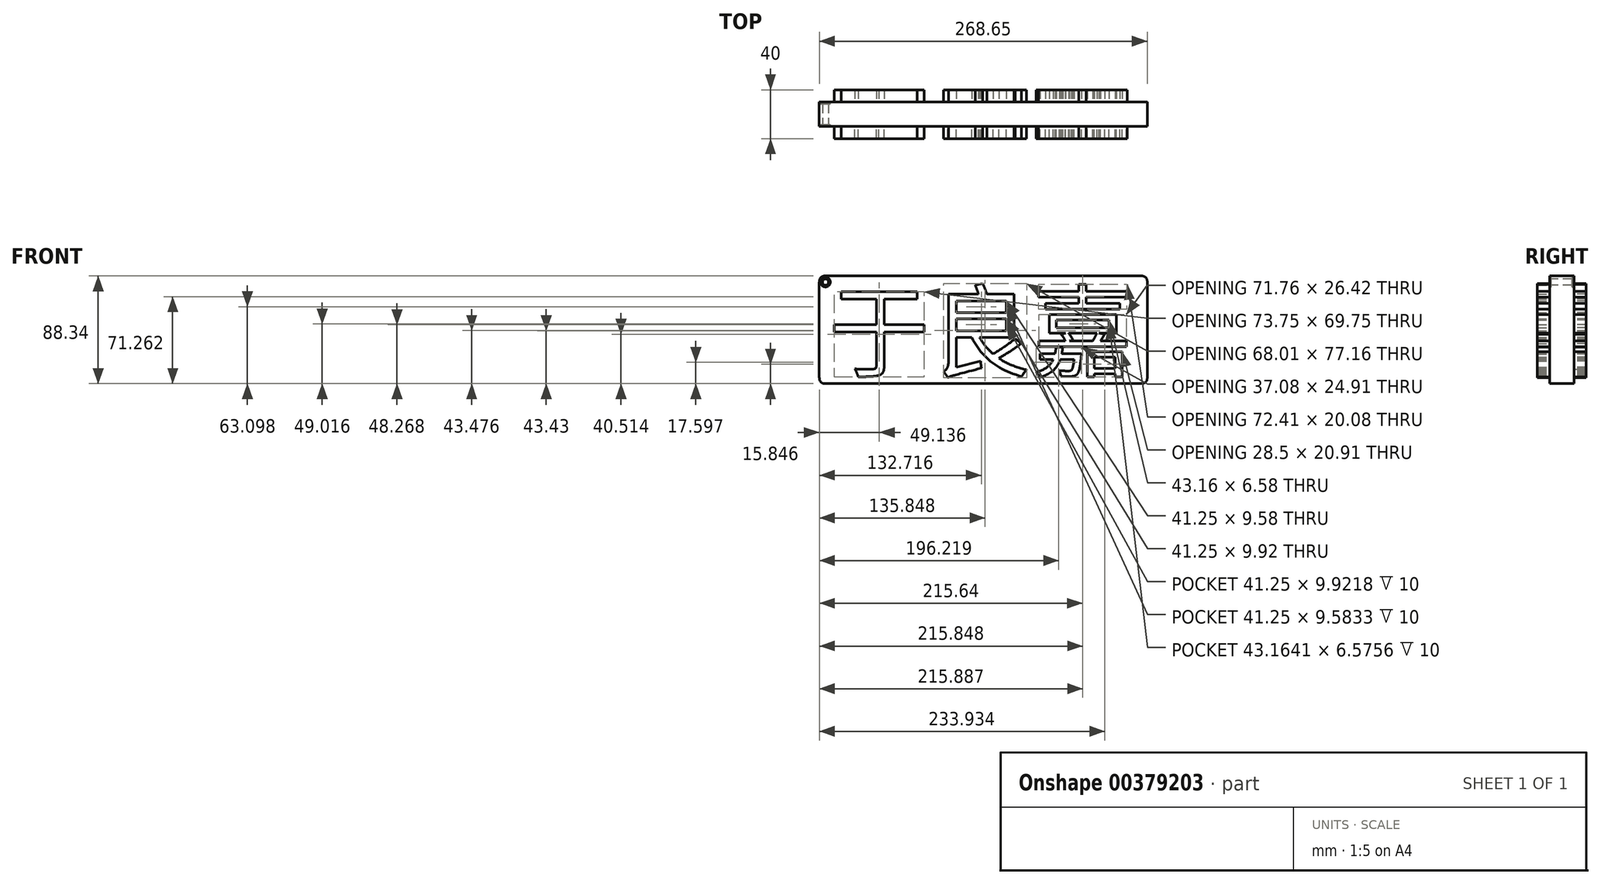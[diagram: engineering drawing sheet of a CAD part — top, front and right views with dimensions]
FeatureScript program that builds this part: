
annotation { "Feature Type Name" : "Feature", "Feature Type Description" : "" }
export const myFeature = defineFeature(function(context is Context, id is Id, definition is map)
    precondition{}
    {
        {
            var Q0;
            Q0=qCreatedBy(makeId("Front.planeOp"),FACE);
            var sketch = newSketch(context, id + "F0", { "sketchPlane" : qUnion([Q0])});
            skText(sketch, "E0", { "text": "于良嘉", "fontName": "NotoSansCJKtc-Regular.otf"});
            const initialGuessF0  = {"E0": [-0.12466, -0.0336, 1, 0, 0.06]};
            skSetInitialGuess(sketch, initialGuessF0);
            skSolve(sketch);
        }
        {
            var Q0;
            Q0 = qSketchRegion(id + "F0", true);
            extrude(context, id + "F1", {"entities" : qUnion([Q0]), "depth" : 20 * mm});
        }
        {
            var Q0;
            Q0=qCreatedBy(makeId("Front.planeOp"),FACE);
            var sketch = newSketch(context, id + "F2", { "sketchPlane" : qUnion([Q0])});
            skLineSegment(sketch, "E1.bottom", {"start": v(-132.1, 43.1) * mm, "end": v(136.56, 43.1) * mm});
            skLineSegment(sketch, "E1.top", {"start": v(-132.1, -45.24) * mm, "end": v(136.56, -45.24) * mm});
            skLineSegment(sketch, "E1.left", {"start": v(-132.1, 43.1) * mm, "end": v(-132.1, -45.24) * mm});
            skLineSegment(sketch, "E1.right", {"start": v(136.56, 43.1) * mm, "end": v(136.56, -45.24) * mm});
            skSolve(sketch);
        }
        {
            var Q0;
            Q0=makeQuery(id+"F2.imprint","IMPRINT",FACE,{"disambiguationData":[TD([[makeQuery(id+"F2.imprint","IMPRINT",EDGE,{"derivedFrom":sQuery(id+"F2.wireOp",EDGE,"E1.bottom")}),-1.0]])]});
            extrude(context, id + "F3", {"entities" : qUnion([Q0]), "depth" : 10 * mm});
        }
        {
            var Q0;
            Q0=makeQuery(id+"F3.opExtrude","SWEPT_EDGE",EDGE,{"disambiguationData":[OSD([sQuery(id+"F2.wireOp",EDGE,"E1.top"),sQuery(id+"F2.wireOp",EDGE,"E1.left")])]});
            fillet(context, id + "F4", {"entities" : qUnion([Q0]), "radius" : 5.08 * mm, "tangentPropagation" : true, "rho" : 0.5, "crossSection" : FilletCrossSection.CONIC, "allowEdgeOverflow" : false});
        }
        {
            var Q0;
            Q0=makeQuery(id+"F3.opExtrude","SWEPT_EDGE",EDGE,{"disambiguationData":[OSD([sQuery(id+"F2.wireOp",EDGE,"E1.bottom"),sQuery(id+"F2.wireOp",EDGE,"E1.left")])]});
            fillet(context, id + "F5", {"entities" : qUnion([Q0]), "radius" : 5.08 * mm, "tangentPropagation" : true, "rho" : 0.5, "crossSection" : FilletCrossSection.CONIC, "allowEdgeOverflow" : false});
        }
        {
            var Q0;
            Q0=makeQuery(id+"F3.opExtrude","SWEPT_EDGE",EDGE,{"disambiguationData":[OSD([sQuery(id+"F2.wireOp",EDGE,"E1.top"),sQuery(id+"F2.wireOp",EDGE,"E1.right")])]});
            fillet(context, id + "F6", {"entities" : qUnion([Q0]), "radius" : 5.08 * mm, "tangentPropagation" : true, "rho" : 0.5, "crossSection" : FilletCrossSection.CONIC, "allowEdgeOverflow" : false});
        }
        {
            var Q0;
            Q0=makeQuery(id+"F3.opExtrude","SWEPT_EDGE",EDGE,{"disambiguationData":[OSD([sQuery(id+"F2.wireOp",EDGE,"E1.bottom"),sQuery(id+"F2.wireOp",EDGE,"E1.right")])]});
            fillet(context, id + "F7", {"entities" : qUnion([Q0]), "radius" : 5.08 * mm, "tangentPropagation" : true, "rho" : 0.5, "crossSection" : FilletCrossSection.CONIC, "allowEdgeOverflow" : false});
        }
        {
            var Q0;
            Q0=makeQuery(id+"F1.opExtrude","SWEPT_BODY",BODY,{"disambiguationData":[OSD([sQuery(id+"F0.wireOp",EDGE,"E0.sketch_text.stroke-69"),sQuery(id+"F0.wireOp",EDGE,"E0.sketch_text.stroke-70"),sQuery(id+"F0.wireOp",EDGE,"E0.sketch_text.stroke-71"),sQuery(id+"F0.wireOp",EDGE,"E0.sketch_text.stroke-72"),sQuery(id+"F0.wireOp",EDGE,"E0.sketch_text.stroke-73"),sQuery(id+"F0.wireOp",EDGE,"E0.sketch_text.stroke-74"),sQuery(id+"F0.wireOp",EDGE,"E0.sketch_text.stroke-75"),sQuery(id+"F0.wireOp",EDGE,"E0.sketch_text.stroke-76"),sQuery(id+"F0.wireOp",EDGE,"E0.sketch_text.stroke-77"),sQuery(id+"F0.wireOp",EDGE,"E0.sketch_text.stroke-78"),sQuery(id+"F0.wireOp",EDGE,"E0.sketch_text.stroke-79"),sQuery(id+"F0.wireOp",EDGE,"E0.sketch_text.stroke-80")])]});
            var Q1;
            Q1=makeQuery(id+"F1.opExtrude","SWEPT_BODY",BODY,{"disambiguationData":[OSD([sQuery(id+"F0.wireOp",EDGE,"E0.sketch_text.stroke-81"),sQuery(id+"F0.wireOp",EDGE,"E0.sketch_text.stroke-82"),sQuery(id+"F0.wireOp",EDGE,"E0.sketch_text.stroke-83"),sQuery(id+"F0.wireOp",EDGE,"E0.sketch_text.stroke-84"),sQuery(id+"F0.wireOp",EDGE,"E0.sketch_text.stroke-85"),sQuery(id+"F0.wireOp",EDGE,"E0.sketch_text.stroke-86"),sQuery(id+"F0.wireOp",EDGE,"E0.sketch_text.stroke-87"),sQuery(id+"F0.wireOp",EDGE,"E0.sketch_text.stroke-88"),sQuery(id+"F0.wireOp",EDGE,"E0.sketch_text.stroke-89"),sQuery(id+"F0.wireOp",EDGE,"E0.sketch_text.stroke-90"),sQuery(id+"F0.wireOp",EDGE,"E0.sketch_text.stroke-91"),sQuery(id+"F0.wireOp",EDGE,"E0.sketch_text.stroke-92"),sQuery(id+"F0.wireOp",EDGE,"E0.sketch_text.stroke-93"),sQuery(id+"F0.wireOp",EDGE,"E0.sketch_text.stroke-94"),sQuery(id+"F0.wireOp",EDGE,"E0.sketch_text.stroke-95"),sQuery(id+"F0.wireOp",EDGE,"E0.sketch_text.stroke-96"),sQuery(id+"F0.wireOp",EDGE,"E0.sketch_text.stroke-97"),sQuery(id+"F0.wireOp",EDGE,"E0.sketch_text.stroke-98"),sQuery(id+"F0.wireOp",EDGE,"E0.sketch_text.stroke-99"),sQuery(id+"F0.wireOp",EDGE,"E0.sketch_text.stroke-100"),sQuery(id+"F0.wireOp",EDGE,"E0.sketch_text.stroke-101"),sQuery(id+"F0.wireOp",EDGE,"E0.sketch_text.stroke-102"),sQuery(id+"F0.wireOp",EDGE,"E0.sketch_text.stroke-103")])]});
            var Q2;
            Q2=makeQuery(id+"F1.opExtrude","SWEPT_BODY",BODY,{"disambiguationData":[OSD([sQuery(id+"F0.wireOp",EDGE,"E0.sketch_text.stroke-104"),sQuery(id+"F0.wireOp",EDGE,"E0.sketch_text.stroke-105"),sQuery(id+"F0.wireOp",EDGE,"E0.sketch_text.stroke-106"),sQuery(id+"F0.wireOp",EDGE,"E0.sketch_text.stroke-107"),sQuery(id+"F0.wireOp",EDGE,"E0.sketch_text.stroke-108"),sQuery(id+"F0.wireOp",EDGE,"E0.sketch_text.stroke-109"),sQuery(id+"F0.wireOp",EDGE,"E0.sketch_text.stroke-110"),sQuery(id+"F0.wireOp",EDGE,"E0.sketch_text.stroke-111"),sQuery(id+"F0.wireOp",EDGE,"E0.sketch_text.stroke-112"),sQuery(id+"F0.wireOp",EDGE,"E0.sketch_text.stroke-113"),sQuery(id+"F0.wireOp",EDGE,"E0.sketch_text.stroke-114"),sQuery(id+"F0.wireOp",EDGE,"E0.sketch_text.stroke-115"),sQuery(id+"F0.wireOp",EDGE,"E0.sketch_text.stroke-116"),sQuery(id+"F0.wireOp",EDGE,"E0.sketch_text.stroke-117"),sQuery(id+"F0.wireOp",EDGE,"E0.sketch_text.stroke-118"),sQuery(id+"F0.wireOp",EDGE,"E0.sketch_text.stroke-119")])]});
            var Q3;
            Q3=makeQuery(id+"F3.opExtrude","SWEPT_BODY",BODY,{"disambiguationData":[OSD([sQuery(id+"F2.wireOp",EDGE,"E1.bottom"),sQuery(id+"F2.wireOp",EDGE,"E1.top"),sQuery(id+"F2.wireOp",EDGE,"E1.left"),sQuery(id+"F2.wireOp",EDGE,"E1.right")])]});
            var Q4;
            Q4=makeQuery(id+"F1.opExtrude","SWEPT_BODY",BODY,{"disambiguationData":[OSD([sQuery(id+"F0.wireOp",EDGE,"E0.sketch_text.stroke-50"),sQuery(id+"F0.wireOp",EDGE,"E0.sketch_text.stroke-51"),sQuery(id+"F0.wireOp",EDGE,"E0.sketch_text.stroke-52"),sQuery(id+"F0.wireOp",EDGE,"E0.sketch_text.stroke-53"),sQuery(id+"F0.wireOp",EDGE,"E0.sketch_text.stroke-54"),sQuery(id+"F0.wireOp",EDGE,"E0.sketch_text.stroke-55"),sQuery(id+"F0.wireOp",EDGE,"E0.sketch_text.stroke-56"),sQuery(id+"F0.wireOp",EDGE,"E0.sketch_text.stroke-57"),sQuery(id+"F0.wireOp",EDGE,"E0.sketch_text.stroke-58"),sQuery(id+"F0.wireOp",EDGE,"E0.sketch_text.stroke-59"),sQuery(id+"F0.wireOp",EDGE,"E0.sketch_text.stroke-60"),sQuery(id+"F0.wireOp",EDGE,"E0.sketch_text.stroke-61"),sQuery(id+"F0.wireOp",EDGE,"E0.sketch_text.stroke-62"),sQuery(id+"F0.wireOp",EDGE,"E0.sketch_text.stroke-63"),sQuery(id+"F0.wireOp",EDGE,"E0.sketch_text.stroke-64"),sQuery(id+"F0.wireOp",EDGE,"E0.sketch_text.stroke-65"),sQuery(id+"F0.wireOp",EDGE,"E0.sketch_text.stroke-66"),sQuery(id+"F0.wireOp",EDGE,"E0.sketch_text.stroke-67"),sQuery(id+"F0.wireOp",EDGE,"E0.sketch_text.stroke-68")])]});
            var Q5;
            Q5=makeQuery(id+"F1.opExtrude","SWEPT_BODY",BODY,{"disambiguationData":[OSD([sQuery(id+"F0.wireOp",EDGE,"E0.sketch_text.stroke-20"),sQuery(id+"F0.wireOp",EDGE,"E0.sketch_text.stroke-21"),sQuery(id+"F0.wireOp",EDGE,"E0.sketch_text.stroke-22"),sQuery(id+"F0.wireOp",EDGE,"E0.sketch_text.stroke-23"),sQuery(id+"F0.wireOp",EDGE,"E0.sketch_text.stroke-24"),sQuery(id+"F0.wireOp",EDGE,"E0.sketch_text.stroke-25"),sQuery(id+"F0.wireOp",EDGE,"E0.sketch_text.stroke-26"),sQuery(id+"F0.wireOp",EDGE,"E0.sketch_text.stroke-27"),sQuery(id+"F0.wireOp",EDGE,"E0.sketch_text.stroke-28"),sQuery(id+"F0.wireOp",EDGE,"E0.sketch_text.stroke-29"),sQuery(id+"F0.wireOp",EDGE,"E0.sketch_text.stroke-30"),sQuery(id+"F0.wireOp",EDGE,"E0.sketch_text.stroke-31"),sQuery(id+"F0.wireOp",EDGE,"E0.sketch_text.stroke-32"),sQuery(id+"F0.wireOp",EDGE,"E0.sketch_text.stroke-33"),sQuery(id+"F0.wireOp",EDGE,"E0.sketch_text.stroke-34"),sQuery(id+"F0.wireOp",EDGE,"E0.sketch_text.stroke-35"),sQuery(id+"F0.wireOp",EDGE,"E0.sketch_text.stroke-36"),sQuery(id+"F0.wireOp",EDGE,"E0.sketch_text.stroke-37"),sQuery(id+"F0.wireOp",EDGE,"E0.sketch_text.stroke-38"),sQuery(id+"F0.wireOp",EDGE,"E0.sketch_text.stroke-39"),sQuery(id+"F0.wireOp",EDGE,"E0.sketch_text.stroke-40"),sQuery(id+"F0.wireOp",EDGE,"E0.sketch_text.stroke-41"),sQuery(id+"F0.wireOp",EDGE,"E0.sketch_text.stroke-42"),sQuery(id+"F0.wireOp",EDGE,"E0.sketch_text.stroke-43"),sQuery(id+"F0.wireOp",EDGE,"E0.sketch_text.stroke-44"),sQuery(id+"F0.wireOp",EDGE,"E0.sketch_text.stroke-45"),sQuery(id+"F0.wireOp",EDGE,"E0.sketch_text.stroke-46"),sQuery(id+"F0.wireOp",EDGE,"E0.sketch_text.stroke-47"),sQuery(id+"F0.wireOp",EDGE,"E0.sketch_text.stroke-48"),sQuery(id+"F0.wireOp",EDGE,"E0.sketch_text.stroke-49")])]});
            var Q6;
            Q6=makeQuery(id+"F1.opExtrude","SWEPT_BODY",BODY,{"disambiguationData":[OSD([sQuery(id+"F0.wireOp",EDGE,"E0.sketch_text.stroke-0"),sQuery(id+"F0.wireOp",EDGE,"E0.sketch_text.stroke-1"),sQuery(id+"F0.wireOp",EDGE,"E0.sketch_text.stroke-2"),sQuery(id+"F0.wireOp",EDGE,"E0.sketch_text.stroke-3"),sQuery(id+"F0.wireOp",EDGE,"E0.sketch_text.stroke-4"),sQuery(id+"F0.wireOp",EDGE,"E0.sketch_text.stroke-5"),sQuery(id+"F0.wireOp",EDGE,"E0.sketch_text.stroke-6"),sQuery(id+"F0.wireOp",EDGE,"E0.sketch_text.stroke-7"),sQuery(id+"F0.wireOp",EDGE,"E0.sketch_text.stroke-8"),sQuery(id+"F0.wireOp",EDGE,"E0.sketch_text.stroke-9"),sQuery(id+"F0.wireOp",EDGE,"E0.sketch_text.stroke-10"),sQuery(id+"F0.wireOp",EDGE,"E0.sketch_text.stroke-11"),sQuery(id+"F0.wireOp",EDGE,"E0.sketch_text.stroke-12"),sQuery(id+"F0.wireOp",EDGE,"E0.sketch_text.stroke-13"),sQuery(id+"F0.wireOp",EDGE,"E0.sketch_text.stroke-14"),sQuery(id+"F0.wireOp",EDGE,"E0.sketch_text.stroke-15"),sQuery(id+"F0.wireOp",EDGE,"E0.sketch_text.stroke-16"),sQuery(id+"F0.wireOp",EDGE,"E0.sketch_text.stroke-17"),sQuery(id+"F0.wireOp",EDGE,"E0.sketch_text.stroke-18"),sQuery(id+"F0.wireOp",EDGE,"E0.sketch_text.stroke-19")])]});
            booleanBodies(context, id + "F8", {"operationType" : BooleanOperationType.UNION, "tools" : qUnion([Q0, Q1, Q2, Q3, Q4, Q5, Q6])});
        }
        {
            var Q0;
            {var subQ0=sQuery(id+"F2.wireOp",EDGE,"E1.right");var subQ1=sQuery(id+"F2.wireOp",EDGE,"E1.bottom");var subQ2=sQuery(id+"F2.wireOp",EDGE,"E1.top");var subQ3=sQuery(id+"F2.wireOp",EDGE,"E1.left");Q0=makeQuery(id+"F8.opBoolean","SPLIT",FACE,{"disambiguationData":[TD([makeQuery(id+"F1.opExtrude","SWEPT_FACE",FACE,{"disambiguationData":[OSD([sQuery(id+"F0.wireOp",EDGE,"E0.sketch_text.stroke-0")])]})])],"derivedFrom":makeQuery(id+"F3.opExtrude","CAP_FACE",FACE,{"disambiguationData":[OSD([subQ1,subQ2,subQ3,subQ0])],"isStart":false})});}
            var sketch = newSketch(context, id + "F9", { "sketchPlane" : qUnion([Q0])});
            skCircle(sketch, "E2", {"center": v(-127.01, 38.04) * mm, "radius": 2.84 * mm});
            skSolve(sketch);
        }
        {
            var Q0;
            Q0=sQuery(id+"F9.wireOp",VERTEX,"E2.center");
            var Q1;
            Q1=makeQuery(id+"F1.opExtrude","SWEPT_BODY",BODY,{"disambiguationData":[OSD([sQuery(id+"F0.wireOp",EDGE,"E0.sketch_text.stroke-69"),sQuery(id+"F0.wireOp",EDGE,"E0.sketch_text.stroke-70"),sQuery(id+"F0.wireOp",EDGE,"E0.sketch_text.stroke-71"),sQuery(id+"F0.wireOp",EDGE,"E0.sketch_text.stroke-72"),sQuery(id+"F0.wireOp",EDGE,"E0.sketch_text.stroke-73"),sQuery(id+"F0.wireOp",EDGE,"E0.sketch_text.stroke-74"),sQuery(id+"F0.wireOp",EDGE,"E0.sketch_text.stroke-75"),sQuery(id+"F0.wireOp",EDGE,"E0.sketch_text.stroke-76"),sQuery(id+"F0.wireOp",EDGE,"E0.sketch_text.stroke-77"),sQuery(id+"F0.wireOp",EDGE,"E0.sketch_text.stroke-78"),sQuery(id+"F0.wireOp",EDGE,"E0.sketch_text.stroke-79"),sQuery(id+"F0.wireOp",EDGE,"E0.sketch_text.stroke-80")])]});
            hole(context, id + "F10", {"style" : HoleStyle.C_BORE, "endStyle" : HoleEndStyle.THROUGH, "holeDiameter" : 5 * mm, "cBoreDiameter" : 8 * mm, "cBoreDepth" : 1.5 * mm, "isTappedThrough" : true, "tappedDepth" : 12.7 * mm, "tapClearance" : 3, "startFromSketch" : true, "locations" : qUnion([Q0]), "scope" : qUnion([Q1])});
        }
        {
            var Q0;
            Q0=makeQuery(id+"F1.opExtrude","SWEPT_BODY",BODY,{"disambiguationData":[OSD([sQuery(id+"F0.wireOp",EDGE,"E0.sketch_text.stroke-69"),sQuery(id+"F0.wireOp",EDGE,"E0.sketch_text.stroke-70"),sQuery(id+"F0.wireOp",EDGE,"E0.sketch_text.stroke-71"),sQuery(id+"F0.wireOp",EDGE,"E0.sketch_text.stroke-72"),sQuery(id+"F0.wireOp",EDGE,"E0.sketch_text.stroke-73"),sQuery(id+"F0.wireOp",EDGE,"E0.sketch_text.stroke-74"),sQuery(id+"F0.wireOp",EDGE,"E0.sketch_text.stroke-75"),sQuery(id+"F0.wireOp",EDGE,"E0.sketch_text.stroke-76"),sQuery(id+"F0.wireOp",EDGE,"E0.sketch_text.stroke-77"),sQuery(id+"F0.wireOp",EDGE,"E0.sketch_text.stroke-78"),sQuery(id+"F0.wireOp",EDGE,"E0.sketch_text.stroke-79"),sQuery(id+"F0.wireOp",EDGE,"E0.sketch_text.stroke-80")])]});
            var Q1;
            Q1=makeQuery(id+"F8.opBoolean","MERGE",FACE,{"derivedFrom":[makeQuery(id+"F1.opExtrude","CAP_FACE",FACE,{"disambiguationData":[OSD([sQuery(id+"F0.wireOp",EDGE,"E0.sketch_text.stroke-69"),sQuery(id+"F0.wireOp",EDGE,"E0.sketch_text.stroke-70"),sQuery(id+"F0.wireOp",EDGE,"E0.sketch_text.stroke-71"),sQuery(id+"F0.wireOp",EDGE,"E0.sketch_text.stroke-72"),sQuery(id+"F0.wireOp",EDGE,"E0.sketch_text.stroke-73"),sQuery(id+"F0.wireOp",EDGE,"E0.sketch_text.stroke-74"),sQuery(id+"F0.wireOp",EDGE,"E0.sketch_text.stroke-75"),sQuery(id+"F0.wireOp",EDGE,"E0.sketch_text.stroke-76"),sQuery(id+"F0.wireOp",EDGE,"E0.sketch_text.stroke-77"),sQuery(id+"F0.wireOp",EDGE,"E0.sketch_text.stroke-78"),sQuery(id+"F0.wireOp",EDGE,"E0.sketch_text.stroke-79"),sQuery(id+"F0.wireOp",EDGE,"E0.sketch_text.stroke-80")])],"isStart":true}),makeQuery(id+"F1.opExtrude","CAP_FACE",FACE,{"disambiguationData":[OSD([sQuery(id+"F0.wireOp",EDGE,"E0.sketch_text.stroke-81"),sQuery(id+"F0.wireOp",EDGE,"E0.sketch_text.stroke-82"),sQuery(id+"F0.wireOp",EDGE,"E0.sketch_text.stroke-83"),sQuery(id+"F0.wireOp",EDGE,"E0.sketch_text.stroke-84"),sQuery(id+"F0.wireOp",EDGE,"E0.sketch_text.stroke-85"),sQuery(id+"F0.wireOp",EDGE,"E0.sketch_text.stroke-86"),sQuery(id+"F0.wireOp",EDGE,"E0.sketch_text.stroke-87"),sQuery(id+"F0.wireOp",EDGE,"E0.sketch_text.stroke-88"),sQuery(id+"F0.wireOp",EDGE,"E0.sketch_text.stroke-89"),sQuery(id+"F0.wireOp",EDGE,"E0.sketch_text.stroke-90"),sQuery(id+"F0.wireOp",EDGE,"E0.sketch_text.stroke-91"),sQuery(id+"F0.wireOp",EDGE,"E0.sketch_text.stroke-92"),sQuery(id+"F0.wireOp",EDGE,"E0.sketch_text.stroke-93"),sQuery(id+"F0.wireOp",EDGE,"E0.sketch_text.stroke-94"),sQuery(id+"F0.wireOp",EDGE,"E0.sketch_text.stroke-95"),sQuery(id+"F0.wireOp",EDGE,"E0.sketch_text.stroke-96"),sQuery(id+"F0.wireOp",EDGE,"E0.sketch_text.stroke-97"),sQuery(id+"F0.wireOp",EDGE,"E0.sketch_text.stroke-98"),sQuery(id+"F0.wireOp",EDGE,"E0.sketch_text.stroke-99"),sQuery(id+"F0.wireOp",EDGE,"E0.sketch_text.stroke-100"),sQuery(id+"F0.wireOp",EDGE,"E0.sketch_text.stroke-101"),sQuery(id+"F0.wireOp",EDGE,"E0.sketch_text.stroke-102"),sQuery(id+"F0.wireOp",EDGE,"E0.sketch_text.stroke-103")])],"isStart":true}),makeQuery(id+"F1.opExtrude","CAP_FACE",FACE,{"disambiguationData":[OSD([sQuery(id+"F0.wireOp",EDGE,"E0.sketch_text.stroke-104"),sQuery(id+"F0.wireOp",EDGE,"E0.sketch_text.stroke-105"),sQuery(id+"F0.wireOp",EDGE,"E0.sketch_text.stroke-106"),sQuery(id+"F0.wireOp",EDGE,"E0.sketch_text.stroke-107"),sQuery(id+"F0.wireOp",EDGE,"E0.sketch_text.stroke-108"),sQuery(id+"F0.wireOp",EDGE,"E0.sketch_text.stroke-109"),sQuery(id+"F0.wireOp",EDGE,"E0.sketch_text.stroke-110"),sQuery(id+"F0.wireOp",EDGE,"E0.sketch_text.stroke-111"),sQuery(id+"F0.wireOp",EDGE,"E0.sketch_text.stroke-112"),sQuery(id+"F0.wireOp",EDGE,"E0.sketch_text.stroke-113"),sQuery(id+"F0.wireOp",EDGE,"E0.sketch_text.stroke-114"),sQuery(id+"F0.wireOp",EDGE,"E0.sketch_text.stroke-115"),sQuery(id+"F0.wireOp",EDGE,"E0.sketch_text.stroke-116"),sQuery(id+"F0.wireOp",EDGE,"E0.sketch_text.stroke-117"),sQuery(id+"F0.wireOp",EDGE,"E0.sketch_text.stroke-118"),sQuery(id+"F0.wireOp",EDGE,"E0.sketch_text.stroke-119")])],"isStart":true}),makeQuery(id+"F3.opExtrude","CAP_FACE",FACE,{"disambiguationData":[OSD([sQuery(id+"F2.wireOp",EDGE,"E1.bottom"),sQuery(id+"F2.wireOp",EDGE,"E1.top"),sQuery(id+"F2.wireOp",EDGE,"E1.left"),sQuery(id+"F2.wireOp",EDGE,"E1.right")])],"isStart":true})]});
            mirror(context, id + "F11", {"operationType" : NewBodyOperationType.ADD, "entities" : qUnion([Q0]), "mirrorPlane" : qUnion([Q1])});
        }
    });
